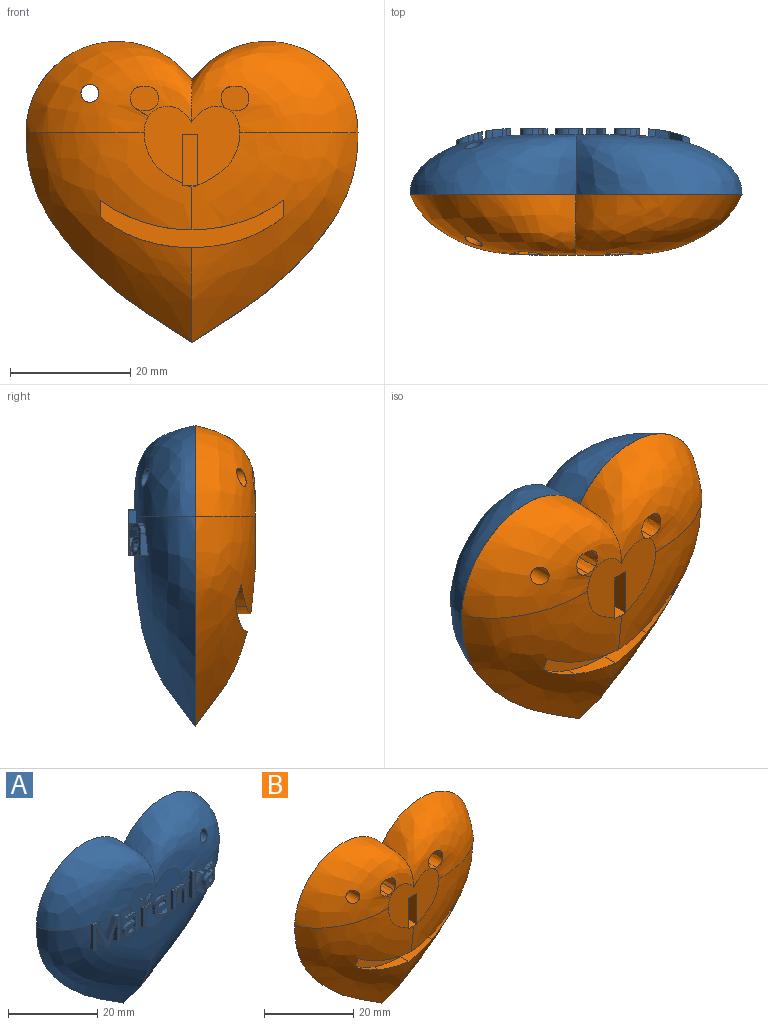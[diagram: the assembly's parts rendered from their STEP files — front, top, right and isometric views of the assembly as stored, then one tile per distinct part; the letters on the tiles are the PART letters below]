
ASSEMBLY  parts=2 mates=1
PART A: 169 faces, bbox 55.8x11.1x50.2 mm
  f0: plane 6.23x2.38mm, normal (-0.93,0,-0.36), area 8.1mm2, adj f1,f16,f21,f159
  f1: plane 1.7x0.67mm, normal (0,0,-1), area 1mm2, adj f0,f2,f21,f159
  f2: plane 6.23x2.42mm, normal (0.93,0,-0.36), area 9.3mm2, adj f1,f3,f21,f159
  f3: plane 1.27x0.04mm, normal (0,0,-1), area 0mm2, adj f2,f4,f21,f159
  f4: extruded ~1.69x1.29mm, area 2.2mm2, adj f3,f5,f21,f159
  f5: plane 4.53x1.55mm, normal (-1,0,0), area 6.3mm2, adj f4,f6,f21,f159
  f6: plane 1.59x0.83mm, normal (0,0,-1), area 1.2mm2, adj f5,f21,f26,f159
  f7: plane 1.37x1.24mm, normal (0,0,1), area 1.5mm2, adj f8,f23,f26,f159
  f8: plane 5.82x2.26mm, normal (-0.93,0,0.36), area 8.3mm2, adj f7,f9,f23,f24,f159
  f9: plane 1.45x0.04mm, normal (0,0,1), area 0.1mm2, adj f8,f10,f24,f159
  f10: plane 5.81x2.24mm, normal (0.93,0,0.36), area 7.5mm2, adj f9,f11,f23,f24,f159
  f11: plane 1.36x1.23mm, normal (0,0,1), area 1.2mm2, adj f10,f12,f23,f159
  f12: plane 7.03x1.37mm, normal (-1,0,0), area 7.2mm2, adj f11,f13,f21,f23,f159
  f13: plane 1.65x0.76mm, normal (0,0,-1), area 1mm2, adj f12,f14,f21,f159
  f14: plane 4.47x1.4mm, normal (1,0,0), area 5.2mm2, adj f13,f15,f21,f159
  f15: extruded ~1.76x1.01mm, area 1.7mm2, adj f14,f16,f21,f159
  f16: plane 0.98x0.04mm, normal (0,0,-1), area 0mm2, adj f0,f15,f21,f159
  f17: bspline ~27.79x15.18mm, area 500.6mm2, adj f18,f19,f23,f25,f124,f125,f126,f156
  f18: bspline ~35x27.85mm, area 727.5mm2, adj f17,f19,f20,f21,f25,f103,f104,f105
  f19: plane 16.04x13.56mm, normal (0,-1,0), area 126.4mm2, adj f17,f18,f21,f23,f36,f37,f38,f56
  f20: plane 4.18x2.22mm, normal (0,-1,0), area 5.2mm2, adj f18,f115,f116,f117,f118
  f21: bspline ~35x27.85mm, area 714.9mm2, adj f0,f1,f2,f3,f4,f5,f6,f12
  f22: plane 1.49x0.64mm, normal (0,-1,0), area 0.5mm2, adj f21,f43,f44,f45,f46
  f23: bspline ~27.79x15.18mm, area 507.6mm2, adj f7,f8,f10,f11,f12,f17,f19,f21
  f24: bspline ~13.41x9.16mm, area 10.9mm2, adj f8,f9,f10,f23
  f25: plane 55.36x50.17mm, normal (0,1,0), area 2011.3mm2, adj f17,f18,f21,f23,f156
  f26: plane 7.04x1.48mm, normal (1,0,0), area 9mm2, adj f6,f7,f21,f23,f159
  f27: extruded ~1.17x1.12mm, area 1.4mm2, adj f28,f53,f54,f55
  f28: extruded ~1.16x0.73mm, area 0.9mm2, adj f27,f29,f54,f55
  f29: extruded ~1.16x0.66mm, area 0.8mm2, adj f28,f30,f54,f55
  f30: extruded ~1.14x0.81mm, area 1.1mm2, adj f29,f31,f54,f55
  f31: extruded ~1.37x1.08mm, area 1.5mm2, adj f30,f32,f54,f55
  f32: plane 1.02x0.8mm, normal (0.04,0,-1), area 0.8mm2, adj f31,f33,f54,f55
  f33: plane 1.01x0.48mm, normal (-1,0,0), area 0.5mm2, adj f32,f53,f54,f55
  f34: plane 1.08x0.78mm, normal (-0.98,0,-0.21), area 0.8mm2, adj f21,f35,f52,f54
  f35: plane 1.06x0.6mm, normal (0,0,-1), area 0.6mm2, adj f21,f34,f36,f54
  f36: plane 3.6x1.03mm, normal (1,0,0), area 3.6mm2, adj f19,f21,f35,f37,f54
  f37: extruded ~1.34x1mm, area 1.5mm2, adj f19,f36,f38,f54
  f38: extruded ~1.4x1mm, area 1.5mm2, adj f19,f21,f37,f39,f54
  f39: extruded ~1.02x0.93mm, area 1mm2, adj f21,f38,f40,f54
  f40: extruded ~1.06x0.85mm, area 1mm2, adj f21,f39,f41,f54
  f41: plane 1.07x0.62mm, normal (-0.93,0,-0.37), area 0.7mm2, adj f21,f40,f42,f54
  f42: extruded ~1.49x1.06mm, area 1.6mm2, adj f21,f41,f43,f54
  f43: extruded ~1x0.85mm, area 0.9mm2, adj f21,f22,f42,f44,f54
  f44: extruded ~1x0.92mm, area 1mm2, adj f22,f43,f45,f54
  f45: plane 1x0.33mm, normal (-1,0,0), area 0.3mm2, adj f22,f44,f46,f54
  f46: plane 1.01x0.9mm, normal (-0.03,0,1), area 0.9mm2, adj f21,f22,f45,f47,f54
  f47: extruded ~2.55x1.67mm, area 3.8mm2, adj f21,f46,f48,f54
  f48: extruded ~1.24x1.15mm, area 1.6mm2, adj f21,f47,f49,f54
  f49: extruded ~1.24x1.23mm, area 1.6mm2, adj f21,f48,f50,f54
  f50: extruded ~1.17x0.98mm, area 1.1mm2, adj f21,f49,f51,f54
  f51: extruded ~1.1x0.79mm, area 1.1mm2, adj f21,f50,f52,f54
  f52: plane 1.03x0.04mm, normal (0,0,-1), area 0mm2, adj f21,f34,f51,f54
  f53: extruded ~1.14x1.04mm, area 1.3mm2, adj f27,f33,f54,f55
  f54: plane 5.45x4.22mm, normal (0,-1,0), area 10.9mm2, adj f27,f28,f29,f30,f31,f32,f33,f34
  f55: bspline ~9.22x9.21mm, area 3.8mm2, adj f27,f28,f29,f30,f31,f32,f33,f53
  f56: extruded ~1x0.63mm, area 0.6mm2, adj f19,f57,f68,f69
  f57: extruded ~1x0.91mm, area 1mm2, adj f19,f56,f58,f69
  f58: extruded ~1x0.79mm, area 1.1mm2, adj f19,f57,f59,f69
  f59: plane 1x0.04mm, normal (0,0,1), area 0mm2, adj f19,f58,f60,f69
  f60: plane 1x0.98mm, normal (1,0,0.09), area 1mm2, adj f19,f59,f61,f69
  f61: plane 1x0.66mm, normal (0,0,1), area 0.7mm2, adj f19,f60,f62,f69
  f62: plane 5.27x1mm, normal (-1,0,0), area 5.3mm2, adj f19,f61,f63,f69
  f63: plane 1x0.8mm, normal (0,0,-1), area 0.8mm2, adj f19,f62,f64,f69
  f64: plane 2.83x1mm, normal (1,0,0), area 2.8mm2, adj f19,f63,f65,f69
  f65: extruded ~1.29x1mm, area 1.4mm2, adj f19,f64,f66,f69
  f66: extruded ~1.09x1mm, area 1.3mm2, adj f19,f65,f67,f69
  f67: extruded ~1x0.58mm, area 0.6mm2, adj f19,f66,f68,f69
  f68: plane 1x0.74mm, normal (0.99,0,-0.15), area 0.7mm2, adj f19,f56,f67,f69
  f69: plane 5.36x3.03mm, normal (0,-1,0), area 5.8mm2, adj f56,f57,f58,f59,f60,f61,f62,f63
  f70: plane 1x0.55mm, normal (0,0,1), area 0.6mm2, adj f19,f71,f80,f81
  f71: plane 1x0.12mm, normal (-1,0,0), area 0.1mm2, adj f19,f70,f72,f81
  f72: extruded ~1x0.96mm, area 1.3mm2, adj f19,f71,f73,f81
  f73: extruded ~1x0.5mm, area 0.6mm2, adj f19,f72,f74,f81
  f74: plane 1x0.8mm, normal (0,0,-1), area 0.8mm2, adj f19,f73,f75,f81
  f75: extruded ~1.13x1mm, area 1.5mm2, adj f19,f74,f76,f81
  f76: plane 1x0.33mm, normal (0.72,0,-0.7), area 0.5mm2, adj f19,f75,f77,f81
  f77: plane 1x0.12mm, normal (1,0,0), area 0.1mm2, adj f19,f76,f78,f81
  f78: plane 1x0.57mm, normal (0,0,1), area 0.6mm2, adj f19,f77,f79,f81
  f79: extruded ~1.06x1mm, area 1.4mm2, adj f19,f78,f80,f81
  f80: extruded ~1.05x1mm, area 1.4mm2, adj f19,f70,f79,f81
  f81: plane 3.24x1.58mm, normal (0,-1,0), area 2.3mm2, adj f70,f71,f72,f73,f74,f75,f76,f77
  f82: extruded ~1.01x1mm, area 1.1mm2, adj f83,f100,f101,f102
  f83: extruded ~1x0.96mm, area 1.1mm2, adj f82,f84,f101,f102
  f84: extruded ~1.16x1mm, area 1.2mm2, adj f83,f85,f101,f102
  f85: plane 2.75x1mm, normal (0,0,1), area 2.8mm2, adj f84,f100,f101,f102
  f86: extruded ~1.84x1mm, area 2mm2, adj f19,f87,f99,f101
  f87: extruded ~1x0.91mm, area 0.9mm2, adj f19,f86,f88,f101
  f88: extruded ~1x0.8mm, area 0.8mm2, adj f19,f87,f89,f101
  f89: plane 1x0.71mm, normal (1,0,0), area 0.7mm2, adj f19,f88,f90,f101
  f90: extruded ~1.68x1mm, area 1.7mm2, adj f19,f89,f91,f101
  f91: extruded ~1.25x1mm, area 1.4mm2, adj f19,f90,f92,f101
  f92: extruded ~1.41x1mm, area 1.5mm2, adj f19,f91,f93,f101
  f93: plane 3.63x1mm, normal (0,0,-1), area 3.6mm2, adj f19,f92,f94,f101
  f94: plane 1x0.5mm, normal (1,0,0), area 0.5mm2, adj f19,f93,f95,f101
  f95: extruded ~1.72x1mm, area 1.9mm2, adj f19,f94,f96,f101
  f96: extruded ~1.57x1mm, area 1.8mm2, adj f19,f95,f97,f101
  f97: extruded ~1.69x1mm, area 1.9mm2, adj f19,f96,f98,f101
  f98: extruded ~2.02x1mm, area 2.2mm2, adj f19,f97,f99,f101
  f99: extruded ~1.97x1mm, area 2.1mm2, adj f19,f86,f98,f101
  f100: extruded ~1.14x1mm, area 1.2mm2, adj f82,f85,f101,f102
  f101: plane 5.46x4.46mm, normal (0,-1,0), area 11.1mm2, adj f82,f83,f84,f85,f86,f87,f88,f89
  f102: plane 2.75x1.56mm, normal (0,-1,0), area 3.5mm2, adj f82,f83,f84,f85,f100
  f103: plane 3.41x1.13mm, normal (-1,0,0), area 3.6mm2, adj f18,f104,f119,f120
  f104: plane 1.19x0.81mm, normal (0,0,-1), area 0.9mm2, adj f18,f103,f105,f120
  f105: plane 3.44x1.19mm, normal (1,0,0), area 3.8mm2, adj f18,f104,f106,f120
  f106: extruded ~1.47x1.04mm, area 1.6mm2, adj f18,f105,f107,f120
  f107: extruded ~1.43x1.01mm, area 1.5mm2, adj f18,f19,f106,f108,f120
  f108: extruded ~1x0.99mm, area 1mm2, adj f19,f107,f109,f120
  f109: extruded ~1x0.69mm, area 0.9mm2, adj f19,f108,f110,f120
  f110: plane 1x0.04mm, normal (0,0,1), area 0mm2, adj f19,f109,f111,f120
  f111: plane 1x0.72mm, normal (0.98,0,0.18), area 0.7mm2, adj f19,f110,f112,f120
  f112: plane 1x0.65mm, normal (0,0,1), area 0.6mm2, adj f19,f111,f113,f120
  f113: plane 5.27x1mm, normal (-1,0,0), area 5.3mm2, adj f19,f112,f114,f120
  f114: plane 1.02x0.8mm, normal (0,0,-1), area 0.8mm2, adj f18,f19,f113,f115,f120
  f115: plane 2.78x1.03mm, normal (1,0,0), area 2.8mm2, adj f18,f20,f114,f116,f120
  f116: extruded ~1.48x1mm, area 1.6mm2, adj f20,f115,f117,f120
  f117: extruded ~1.21x1mm, area 1.3mm2, adj f20,f116,f118,f120
  f118: extruded ~1x0.92mm, area 1mm2, adj f18,f20,f117,f119,f120
  f119: extruded ~1.01x0.96mm, area 1mm2, adj f18,f103,f118,f120
  f120: plane 5.36x4.4mm, normal (0,-1,0), area 10.1mm2, adj f103,f104,f105,f106,f107,f108,f109,f110
  f121: extruded ~1.28x0.77mm, area 1.3mm2, adj f18,f122,f135,f136,f158
  f122: plane 1.25x0.04mm, normal (0,0,1), area 0mm2, adj f18,f121,f123,f136
  f123: extruded ~1.24x0.82mm, area 1mm2, adj f18,f122,f124,f136
  f124: plane 4.01x1.25mm, normal (1,0,0), area 4.7mm2, adj f17,f18,f123,f125,f136
  f125: plane 1.18x0.8mm, normal (0,0,1), area 0.9mm2, adj f17,f124,f126,f136
  f126: plane 7.52x1.37mm, normal (-1,0,0), area 8.7mm2, adj f17,f18,f125,f127,f136
  f127: plane 1.43x0.8mm, normal (0,0,-1), area 1.1mm2, adj f18,f126,f128,f136
  f128: plane 1.97x1.42mm, normal (1,0,0), area 2.7mm2, adj f18,f127,f129,f136
  f129: plane 1.34x0.62mm, normal (0.65,0,-0.76), area 1mm2, adj f18,f128,f130,f136,f158
  f130: plane 2.49x1.87mm, normal (-0.8,0,-0.6), area 4.5mm2, adj f18,f129,f131,f158
  f131: plane 1.77x0.98mm, normal (0,0,-1), area 1.5mm2, adj f18,f130,f132,f158
  f132: plane 3.03x2.29mm, normal (0.8,0,0.6), area 5.5mm2, adj f18,f131,f133,f158
  f133: plane 2.25x2.14mm, normal (0.72,0,-0.69), area 4.1mm2, adj f18,f132,f134,f158
  f134: plane 1.46x0.96mm, normal (0,0,1), area 1.2mm2, adj f18,f133,f135,f158
  f135: plane 1.81x1.71mm, normal (-0.73,0,0.69), area 3.2mm2, adj f18,f121,f134,f158
  f136: plane 7.48x1.17mm, normal (0,-1,0), area 6.2mm2, adj f121,f122,f123,f124,f125,f126,f127,f128
  f137: plane 1.42x0.76mm, normal (-0.98,0,-0.21), area 1mm2, adj f18,f138,f155,f157
  f138: plane 1.58x0.6mm, normal (0,0,-1), area 0.8mm2, adj f18,f137,f139,f157
  f139: plane 3.6x1.31mm, normal (1,0,0), area 3.8mm2, adj f18,f138,f140,f157
  f140: extruded ~1.34x1.09mm, area 1.3mm2, adj f18,f139,f141,f157
  f141: extruded ~1.41x1.4mm, area 1.4mm2, adj f18,f140,f142,f157
  f142: extruded ~1.32x0.93mm, area 1mm2, adj f18,f141,f143,f157
  f143: extruded ~1.36x0.85mm, area 1.1mm2, adj f18,f142,f144,f157
  f144: plane 1.28x0.62mm, normal (-0.93,0,-0.37), area 0.8mm2, adj f18,f143,f145,f157
  f145: extruded ~1.5x1.49mm, area 1.7mm2, adj f18,f144,f146,f157
  f146: extruded ~1.27x0.85mm, area 0.9mm2, adj f18,f145,f147,f157
  f147: extruded ~1.08x0.92mm, area 0.9mm2, adj f18,f146,f148,f157
  f148: plane 0.99x0.33mm, normal (-1,0,0), area 0.3mm2, adj f18,f147,f149,f157
  f149: plane 1.36x0.92mm, normal (-0.03,0,1), area 0.9mm2, adj f18,f148,f150,f157
  f150: extruded ~2.55x1.84mm, area 4.2mm2, adj f18,f149,f151,f157
  f151: extruded ~1.61x1.15mm, area 1.9mm2, adj f18,f150,f152,f157
  f152: extruded ~1.82x1.23mm, area 2mm2, adj f18,f151,f153,f157
  f153: extruded ~1.72x0.98mm, area 1.4mm2, adj f18,f152,f154,f157
  f154: extruded ~1.54x0.79mm, area 1.4mm2, adj f18,f153,f155,f157
  f155: plane 1.25x0.04mm, normal (0,0,-1), area 0mm2, adj f18,f137,f154,f157
  f156: cylinder r=1.5mm len=8.88mm, axis (0,1,0), area 78.2mm2, adj f17,f25
  f157: extruded ~5.45x4.22mm, area 11.6mm2, adj f137,f138,f139,f140,f141,f142,f143,f144
  f158: extruded ~5.27x3.06mm, area 5.1mm2, adj f121,f129,f130,f131,f132,f133,f134,f135
  f159: extruded ~7.03x6.96mm, area 21.8mm2, adj f0,f1,f2,f3,f4,f5,f6,f7
  f160: bspline ~9.16x5.77mm, area 3.9mm2, adj f161,f162,f163,f164,f165,f166,f167,f168
  f161: extruded ~1.25x1.14mm, area 1.5mm2, adj f157,f160,f162,f168
  f162: plane 1.08x0.48mm, normal (-1,0,0), area 0.5mm2, adj f157,f160,f161,f163
  f163: plane 1.36x0.82mm, normal (0.04,0,-1), area 0.9mm2, adj f157,f160,f162,f164
  f164: extruded ~1.57x1.37mm, area 1.7mm2, adj f157,f160,f163,f165
  f165: extruded ~1.38x0.81mm, area 1.3mm2, adj f157,f160,f164,f166
  f166: extruded ~1.48x0.66mm, area 1mm2, adj f157,f160,f165,f167
  f167: extruded ~1.6x0.73mm, area 1.1mm2, adj f157,f160,f166,f168
  f168: extruded ~1.65x1.17mm, area 1.7mm2, adj f157,f160,f161,f167
PART B: 40 faces, bbox 55.5x10.1x50.2 mm
  f0: plane 16.05x13.25mm, normal (0,-1,0), area 140.8mm2, adj f1,f2,f3,f4,f7,f8,f10,f36
  f1: bspline ~35x27.72mm, area 692mm2, adj f0,f2,f4,f5,f6,f9,f13,f14
  f2: bspline ~27.66x15.18mm, area 475.7mm2, adj f0,f1,f3,f5,f32,f33,f34,f35
  f3: bspline ~27.66x15.18mm, area 469.3mm2, adj f0,f2,f4,f5,f23,f24,f25,f26
  f4: bspline ~35x27.66mm, area 691.3mm2, adj f0,f1,f3,f5,f6,f8,f9,f12
  f5: plane 55.36x50.17mm, normal (0,1,0), area 2011.3mm2, adj f1,f2,f3,f4,f39
  f6: plane 1.78x0.33mm, normal (0,-1,0), area 0.3mm2, adj f1,f4,f9
  f7: plane 4x2.6mm, normal (0,0,-1), area 10.4mm2, adj f0,f8,f10,f11
  f8: plane 8.4x4.01mm, normal (1,0,0), area 33.5mm2, adj f0,f4,f7,f9,f11
  f9: plane 4.04x2.64mm, normal (0,0,1), area 10.4mm2, adj f1,f4,f6,f8,f10,f11
  f10: plane 8.39x4mm, normal (-1,0,0), area 33.5mm2, adj f0,f7,f9,f11
  f11: plane 8.39x2.6mm, normal (0,-1,0), area 21.8mm2, adj f7,f8,f9,f10
  f12: extruded ~8.37x2.71mm, area 17.9mm2, adj f4,f13,f21,f22
  f13: extruded ~8.45x2.73mm, area 18.4mm2, adj f1,f4,f12,f14,f22
  f14: extruded ~6.95x3.83mm, area 9.2mm2, adj f1,f13,f15,f22
  f15: plane 2.84x1.8mm, normal (-1,0,0), area 3.5mm2, adj f1,f14,f16,f22
  f16: extruded ~7.24x3.7mm, area 17.5mm2, adj f1,f15,f17,f22
  f17: extruded ~8.12x3.3mm, area 24.2mm2, adj f1,f4,f16,f18,f22
  f18: extruded ~8.02x3.29mm, area 23.8mm2, adj f4,f17,f19,f22
  f19: extruded ~7.14x3.64mm, area 17.1mm2, adj f4,f18,f20,f22
  f20: plane 2.8x1.78mm, normal (1,0,0), area 3.4mm2, adj f4,f19,f21,f22
  f21: extruded ~6.75x3.82mm, area 8.8mm2, adj f4,f12,f20,f22
  f22: plane 30.52x7.91mm, normal (0,-1,0), area 90.7mm2, adj f12,f13,f14,f15,f16,f17,f18,f19
  f23: extruded ~3.73x1.74mm, area 6.7mm2, adj f3,f24,f30,f31
  f24: extruded ~3.53x1.77mm, area 6.7mm2, adj f3,f23,f25,f31
  f25: extruded ~3.66x1.45mm, area 5.7mm2, adj f3,f24,f26,f31
  f26: extruded ~3.86x1.54mm, area 6.4mm2, adj f3,f25,f27,f31
  f27: extruded ~3.98x1.71mm, area 7.2mm2, adj f3,f26,f28,f31
  f28: extruded ~3.99x1.74mm, area 7.4mm2, adj f3,f27,f29,f31
  f29: extruded ~3.99x1.54mm, area 6.7mm2, adj f3,f28,f30,f31
  f30: extruded ~3.92x1.5mm, area 6.3mm2, adj f3,f23,f29,f31
  f31: plane 4.63x4.12mm, normal (0,-1,0), area 15.7mm2, adj f23,f24,f25,f26,f27,f28,f29,f30
  f32: extruded ~3.74x2.31mm, area 12.8mm2, adj f2,f33,f37,f38
  f33: extruded ~3.75x1.77mm, area 7mm2, adj f2,f32,f34,f38
  f34: extruded ~3.93x1.45mm, area 6.1mm2, adj f2,f33,f35,f38
  f35: extruded ~4x1.54mm, area 6.7mm2, adj f2,f34,f36,f38
  f36: extruded ~4x1.71mm, area 7.4mm2, adj f0,f2,f35,f37,f38
  f37: extruded ~3.99x2.31mm, area 13.8mm2, adj f2,f32,f36,f38
  f38: plane 4.61x4.12mm, normal (0,-1,0), area 15.7mm2, adj f32,f33,f34,f35,f36,f37
  f39: cylinder r=1.5mm len=8.23mm, axis (0,-1,0), area 77.6mm2, adj f3,f5
PLACE A rot(axis=(0,0,1),180deg) t=(28.91,-19.9,17.62)mm
PLACE B t=(28.91,-19.9,17.62)mm
MATE fastened A.f25 <-> B.f5  axis (0,-1,0) through (28.97,-19.9,11.11)mm
